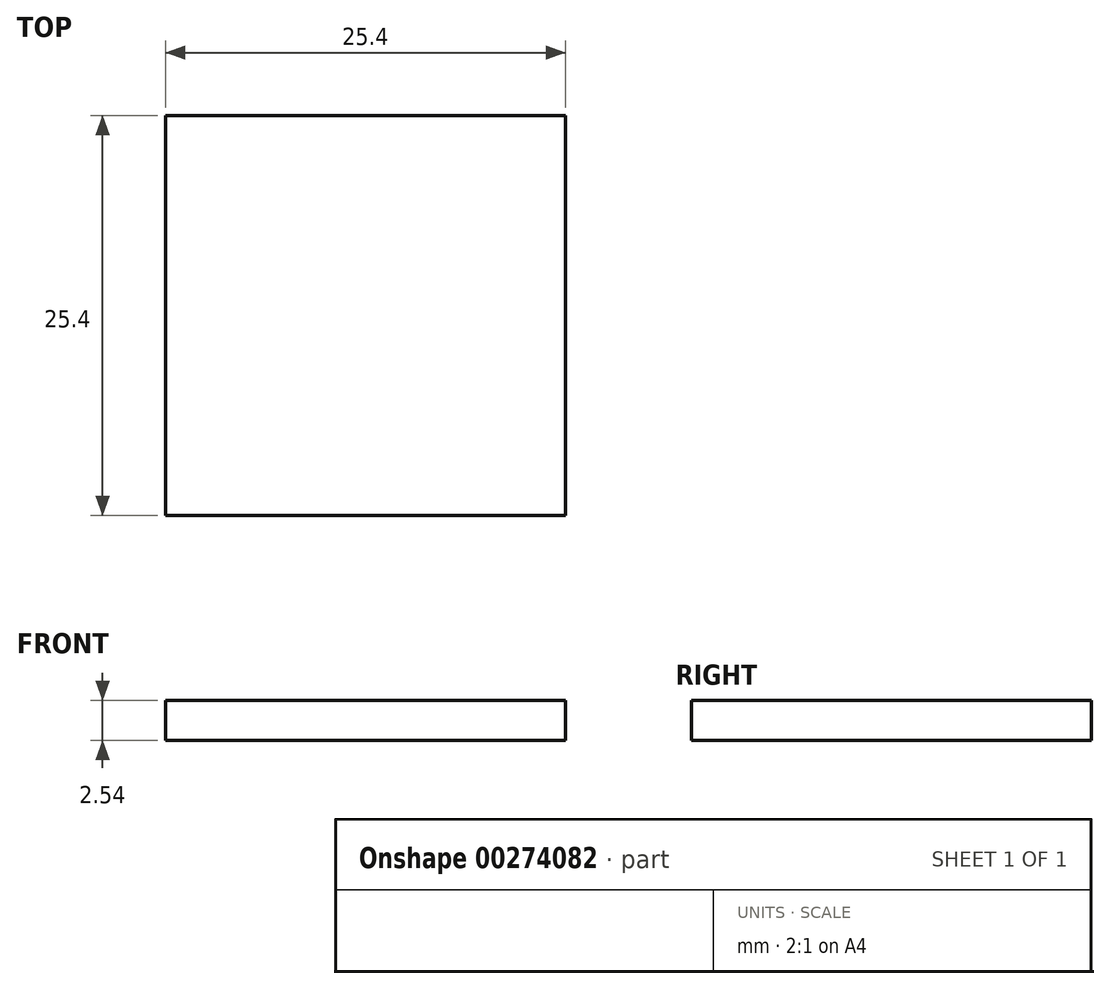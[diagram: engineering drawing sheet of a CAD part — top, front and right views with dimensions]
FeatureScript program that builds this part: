
annotation { "Feature Type Name" : "Feature", "Feature Type Description" : "" }
export const myFeature = defineFeature(function(context is Context, id is Id, definition is map)
    precondition{}
    {
        {
            var Q0;
            Q0=qCreatedBy(makeId("Top.planeOp"),FACE);
            var sketch = newSketch(context, id + "F0", { "sketchPlane" : qUnion([Q0])});
            skLineSegment(sketch, "E0.bottom", {"start": v(12.7, 12.7) * mm, "end": v(-12.7, 12.7) * mm});
            skLineSegment(sketch, "E0.top", {"start": v(12.7, -12.7) * mm, "end": v(-12.7, -12.7) * mm});
            skLineSegment(sketch, "E0.left", {"start": v(12.7, 12.7) * mm, "end": v(12.7, -12.7) * mm});
            skLineSegment(sketch, "E0.right", {"start": v(-12.7, 12.7) * mm, "end": v(-12.7, -12.7) * mm});
            skPoint(sketch, "E0.middle", {"position": v(0, 0) * mm});
            skSolve(sketch);
        }
        {
            var Q0;
            Q0=makeQuery(id+"F0.imprint","IMPRINT",FACE,{"disambiguationData":[TD([[makeQuery(id+"F0.imprint","IMPRINT",EDGE,{"derivedFrom":sQuery(id+"F0.wireOp",EDGE,"E0.bottom")}),1.0]])]});
            extrude(context, id + "F1", {"entities" : qUnion([Q0]), "depth" : 2.54 * mm});
        }
    });
